# Revit family: STS-408К_RV17_LOD_400
name_source: partatom
category: Электрооборудование
revit_build: Autodesk Revit 2017 (Build: 20170118_1100(x64)
units: mm (PartAtom-declared; Revit-internal decimal feet)

## family parameters
Всегда вертикально = Да
Конфигурация панели = Два столбца, слева направо
На основе рабочей плоскости = Нет
Общий = Нет
При загрузке вырезать с полостями = Нет
Размер круглого соединителя = Использовать диаметр
Тип детали = Щит
Точка расчета площади = Нет

## types (1)
- STS-408K
    ADSK_URL страницы изделия = https://stilsoft.ru
    ADSK_Единица измерения = шт.
    ADSK_Завод-изготовитель = ООО «Основа Безопасности»
    ADSK_Количество = 1
    ADSK_Марка = СТВФ.426469.105
    ADSK_Масса = 1.8
    ADSK_Наименование = STS-408K
    ADSK_Размер_Высота = 278 мм
    ADSK_Размер_Глубина = 84 мм
    ADSK_Размер_Ширина = 293 мм
    Интерфейс для подключения внешних = RS-485
    Интерфейс считывающих устройств = Wiegand 26
    Интерфейс считывающих устройств (1) = Wiegand 40/42
    Количество подключаемых = 4
    Количество подключаемых устройств, = 2(4)
    Количество реле, шт. = 4
    Максимальное время работы в = 24
    Максимальное количество = 8
    Максимальное количество ключей = 40000
    Максимальное удаление считывающих = 100 мм
    Максимальный потребляемый контроллером ток от сети переменного тока (без доп. внешних потребителей), А = 0 А
    Максимальный ток, проходящий через реле, не более, А (для 220В) = 2 А
    Максимальный ток, проходящий через реле, не более, А (для 28В) = 4 А
    Напряжение = 220
    Напряжение электропитания переменного однофазного тока, В / Гц = 12
    Стандарт интерфейса связи = 10 Base-T Ethernet (гнездо RJ-45)
